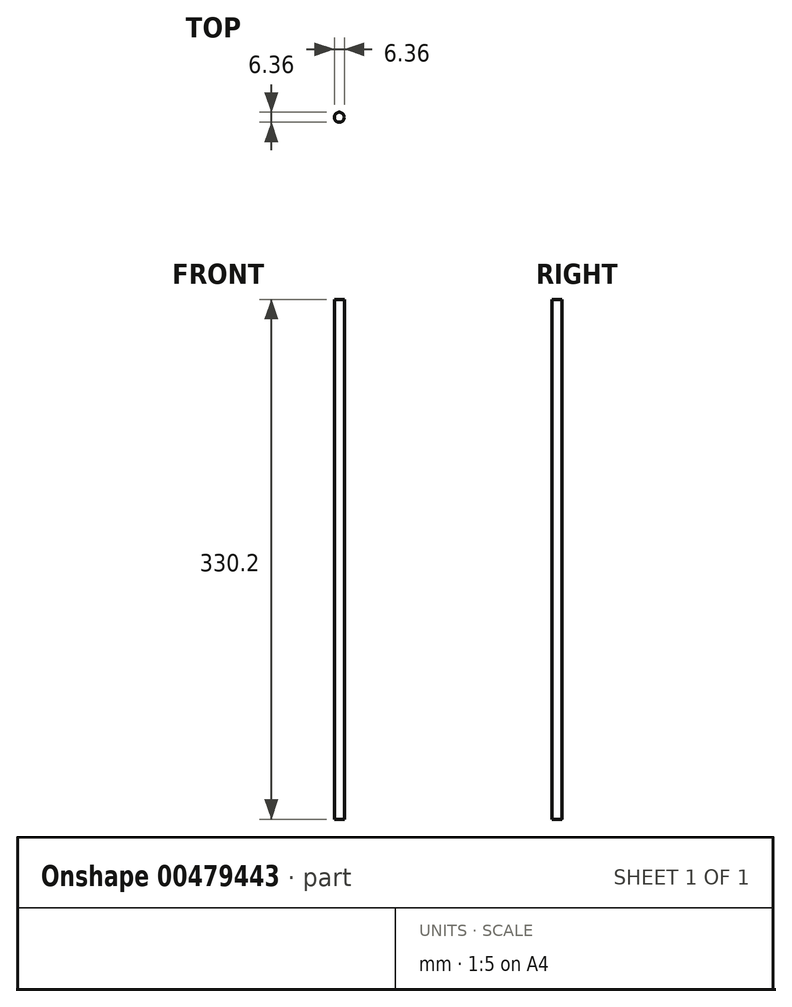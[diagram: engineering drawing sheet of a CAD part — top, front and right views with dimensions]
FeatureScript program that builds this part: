
annotation { "Feature Type Name" : "Feature", "Feature Type Description" : "" }
export const myFeature = defineFeature(function(context is Context, id is Id, definition is map)
    precondition{}
    {
        {
            var Q0;
            Q0=qCreatedBy(makeId("Top.planeOp"),FACE);
            var sketch = newSketch(context, id + "F0", { "sketchPlane" : qUnion([Q0])});
            skCircle(sketch, "E0", {"center": v(0, 0) * mm, "radius": 3.18 * mm});
            skSolve(sketch);
        }
        {
            var Q0;
            Q0=makeQuery(id+"F0.imprint","IMPRINT",FACE,{"disambiguationData":[TD([[makeQuery(id+"F0.imprint","IMPRINT",EDGE,{"derivedFrom":sQuery(id+"F0.wireOp",EDGE,"E0")}),1.0]])]});
            extrude(context, id + "F1", {"entities" : qUnion([Q0]), "depth" : 330.2 * mm, "offsetDistance" : 25.4 * mm});
        }
    });
